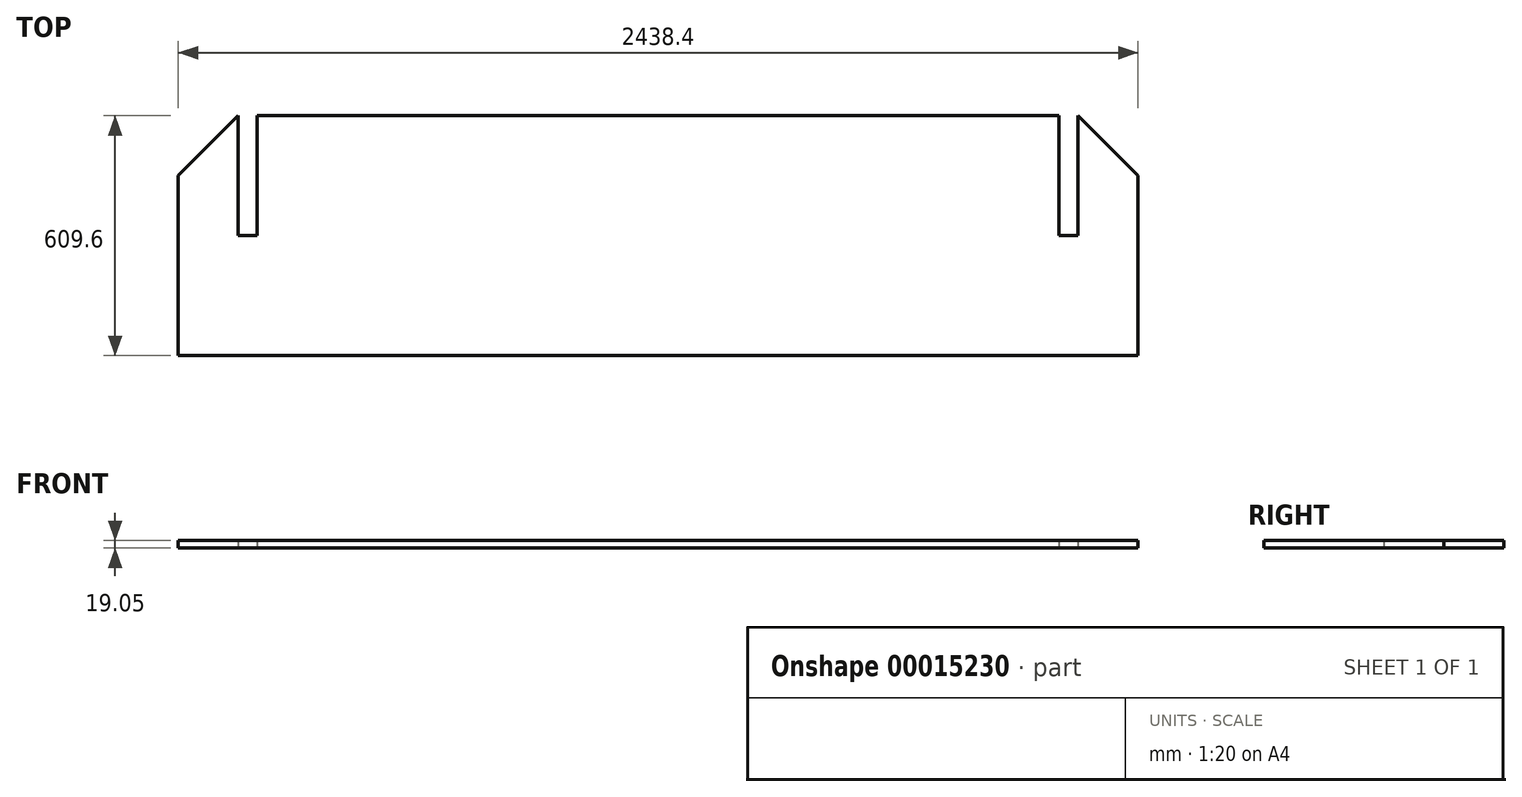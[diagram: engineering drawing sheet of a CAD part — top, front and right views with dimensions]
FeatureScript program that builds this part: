
annotation { "Feature Type Name" : "Feature", "Feature Type Description" : "" }
export const myFeature = defineFeature(function(context is Context, id is Id, definition is map)
    precondition{}
    {
        {
            var Q0;
            Q0=qCreatedBy(makeId("Top.planeOp"),FACE);
            var sketch = newSketch(context, id + "F0", { "sketchPlane" : qUnion([Q0])});
            skLineSegment(sketch, "E0.bottom", {"start": v(-1018.54, 215.9) * mm, "end": v(1018.54, 215.9) * mm});
            skLineSegment(sketch, "E0.top", {"start": v(-1219.2, -393.7) * mm, "end": v(1219.2, -393.7) * mm});
            skLineSegment(sketch, "E0.left", {"start": v(-1219.2, 215.9) * mm, "end": v(-1219.2, -393.7) * mm});
            skLineSegment(sketch, "E0.right", {"start": v(1219.2, 215.9) * mm, "end": v(1219.2, -393.7) * mm});
            skLineSegment(sketch, "E1", {"start": v(-1066.8, 215.9) * mm, "end": v(-1219.2, 63.5) * mm});
            skLineSegment(sketch, "E2", {"start": v(1066.8, 215.9) * mm, "end": v(1219.2, 63.5) * mm});
            skLineSegment(sketch, "E3.left", {"start": v(-1066.8, 215.9) * mm, "end": v(-1066.8, -88.9) * mm});
            skLineSegment(sketch, "E3.right", {"start": v(-1018.54, 215.9) * mm, "end": v(-1018.54, -88.9) * mm});
            skLineSegment(sketch, "E4.left", {"start": v(1066.8, 215.9) * mm, "end": v(1066.8, -88.9) * mm});
            skLineSegment(sketch, "E4.right", {"start": v(1018.54, 215.9) * mm, "end": v(1018.54, -88.9) * mm});
            skLineSegment(sketch, "E3.top", {"start": v(-1066.8, -88.9) * mm, "end": v(-1018.54, -88.9) * mm});
            skLineSegment(sketch, "E4.top", {"start": v(1066.8, -88.9) * mm, "end": v(1018.54, -88.9) * mm});
            skSolve(sketch);
        }
        {
            var Q0;
            Q0=makeQuery(id+"F0.imprint","IMPRINT",FACE,{"disambiguationData":[TD([[makeQuery(id+"F0.imprint","IMPRINT",EDGE,{"derivedFrom":sQuery(id+"F0.wireOp",EDGE,"E0.bottom")}),-1.0]])]});
            extrude(context, id + "F1", {"entities" : qUnion([Q0]), "depth" : 19.05 * mm});
        }
    });
